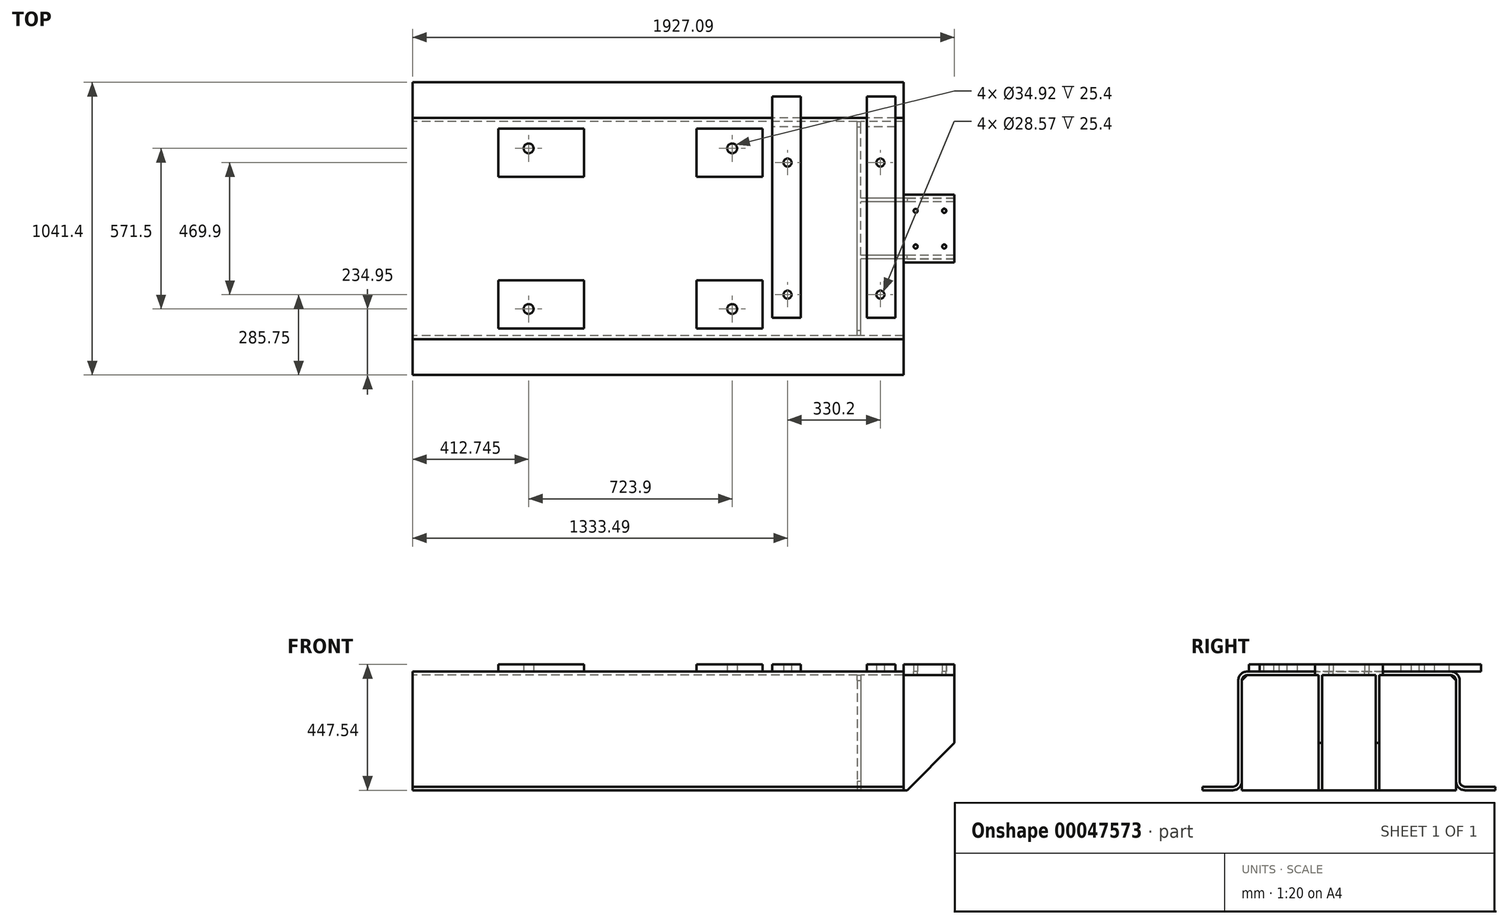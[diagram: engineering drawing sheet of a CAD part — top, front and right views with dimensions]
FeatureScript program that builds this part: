
annotation { "Feature Type Name" : "Feature", "Feature Type Description" : "" }
export const myFeature = defineFeature(function(context is Context, id is Id, definition is map)
    precondition{}
    {
        {
            var Q0;
            Q0=qCreatedBy(makeId("Right.planeOp"),FACE);
            var sketch = newSketch(context, id + "F0", { "sketchPlane" : qUnion([Q0])});
            skLineSegment(sketch, "E0.rect.bottom", {"start": v(-361.95, 211.07) * mm, "end": v(361.95, 211.07) * mm});
            skLineSegment(sketch, "E0.rect.top", {"start": v(-520.7, -211.07) * mm, "end": v(-412.75, -211.07) * mm});
            skLineSegment(sketch, "E0.rect.left", {"start": v(-393.7, 179.32) * mm, "end": v(-393.7, -179.32) * mm});
            skLineSegment(sketch, "E0.rect.right", {"start": v(393.7, 179.32) * mm, "end": v(393.7, -179.32) * mm});
            skPoint(sketch, "E0.rect.middle", {"position": v(0, 0) * mm});
            skLineSegment(sketch, "E1.0", {"start": v(-361.95, 198.37) * mm, "end": v(361.95, 198.37) * mm});
            skLineSegment(sketch, "E1.1", {"start": v(-381, 179.32) * mm, "end": v(-381, -179.32) * mm});
            skLineSegment(sketch, "E1.2", {"start": v(-520.7, -198.37) * mm, "end": v(-412.75, -198.37) * mm});
            skLineSegment(sketch, "E1.3", {"start": v(381, 179.32) * mm, "end": v(381, -179.32) * mm});
            skLineSegment(sketch, "E2.0", {"start": v(-520.7, -198.37) * mm, "end": v(-520.7, -211.07) * mm});
            skLineSegment(sketch, "E3", {"start": v(0, 0) * mm, "end": v(0, 407.59) * mm, "construction": true});
            skPoint(sketch, "E4.orphan", {"position": v(-393.7, -211.07) * mm});
            skLineSegment(sketch, "E5.MirrorCS", {"start": v(520.7, -198.37) * mm, "end": v(520.7, -211.07) * mm});
            skPoint(sketch, "E6.MirrorP", {"position": v(393.7, -211.07) * mm});
            skLineSegment(sketch, "E7.MirrorCS", {"start": v(520.7, -211.07) * mm, "end": v(412.75, -211.07) * mm});
            skLineSegment(sketch, "E8.MirrorCS", {"start": v(520.7, -198.37) * mm, "end": v(412.75, -198.37) * mm});
            skPoint(sketch, "E9.visualSharp", {"position": v(-393.7, -198.37) * mm});
            skArc(sketch, "E9.filletArc", {"start": v(-412.75, -198.37) * mm, "mid": v(-399.28, -192.8) * mm, "end": v(-393.7, -179.32) * mm});
            skPoint(sketch, "E10.visualSharp", {"position": v(-381, 198.37) * mm});
            skArc(sketch, "E10.filletArc", {"start": v(-361.95, 198.37) * mm, "mid": v(-375.42, 192.8) * mm, "end": v(-381, 179.32) * mm});
            skPoint(sketch, "E11.visualSharp", {"position": v(381, 198.37) * mm});
            skArc(sketch, "E11.filletArc", {"start": v(381, 179.32) * mm, "mid": v(375.42, 192.8) * mm, "end": v(361.95, 198.37) * mm});
            skPoint(sketch, "E12.visualSharp", {"position": v(393.7, -198.37) * mm});
            skArc(sketch, "E12.filletArc", {"start": v(393.7, -179.32) * mm, "mid": v(399.28, -192.8) * mm, "end": v(412.75, -198.37) * mm});
            skPoint(sketch, "E13.visualSharp", {"position": v(-381, -211.07) * mm});
            skArc(sketch, "E13.filletArc", {"start": v(-412.75, -211.07) * mm, "mid": v(-390.3, -201.77) * mm, "end": v(-381, -179.32) * mm});
            skPoint(sketch, "E14.visualSharp", {"position": v(-393.7, 211.07) * mm});
            skArc(sketch, "E14.filletArc", {"start": v(-361.95, 211.07) * mm, "mid": v(-384.4, 201.77) * mm, "end": v(-393.7, 179.32) * mm});
            skPoint(sketch, "E15.visualSharp", {"position": v(393.7, 211.07) * mm});
            skArc(sketch, "E15.filletArc", {"start": v(393.7, 179.32) * mm, "mid": v(384.4, 201.77) * mm, "end": v(361.95, 211.07) * mm});
            skPoint(sketch, "E16.visualSharp", {"position": v(381, -211.07) * mm});
            skArc(sketch, "E16.filletArc", {"start": v(381, -179.32) * mm, "mid": v(390.3, -201.77) * mm, "end": v(412.75, -211.07) * mm});
            skSolve(sketch);
        }
        {
            var Q0;
            Q0=qSketchRegion(id+"F0",true);
            extrude(context, id + "F1", {"entities" : qUnion([Q0]), "endBound" : BoundingType.SYMMETRIC, "depth" : 1746.25 * mm});
        }
        {
            var Q0;
            Q0=makeQuery(id+"F1.opExtrude","CAP_FACE",FACE,{"disambiguationData":[OSD([sQuery(id+"F0.wireOp",EDGE,"E0.rect.bottom"),sQuery(id+"F0.wireOp",EDGE,"E0.rect.top"),sQuery(id+"F0.wireOp",EDGE,"E0.rect.left"),sQuery(id+"F0.wireOp",EDGE,"E0.rect.right"),sQuery(id+"F0.wireOp",EDGE,"E1.0"),sQuery(id+"F0.wireOp",EDGE,"E1.1"),sQuery(id+"F0.wireOp",EDGE,"E1.2"),sQuery(id+"F0.wireOp",EDGE,"E1.3"),sQuery(id+"F0.wireOp",EDGE,"E2.0"),sQuery(id+"F0.wireOp",EDGE,"E5.MirrorCS"),sQuery(id+"F0.wireOp",EDGE,"E7.MirrorCS"),sQuery(id+"F0.wireOp",EDGE,"E8.MirrorCS"),sQuery(id+"F0.wireOp",EDGE,"E9.filletArc"),sQuery(id+"F0.wireOp",EDGE,"E10.filletArc"),sQuery(id+"F0.wireOp",EDGE,"E11.filletArc"),sQuery(id+"F0.wireOp",EDGE,"E12.filletArc"),sQuery(id+"F0.wireOp",EDGE,"E13.filletArc"),sQuery(id+"F0.wireOp",EDGE,"E14.filletArc"),sQuery(id+"F0.wireOp",EDGE,"E15.filletArc"),sQuery(id+"F0.wireOp",EDGE,"E16.filletArc")])],"isStart":false});
            cPlane(context, id + "F2", {"entities" : qUnion([Q0]), "cplaneType" : CPlaneType.OFFSET, "offset" : 152.4 * mm, "oppositeDirection" : true, "width" : 152.4 * mm, "height" : 152.4 * mm});
        }
        {
            var Q0;
            Q0=qCreatedBy(id+"F2.planeOp",FACE);
            var sketch = newSketch(context, id + "F3", { "sketchPlane" : qUnion([Q0])});
            skLineSegment(sketch, "E17.0", {"start": v(-361.95, 198.37) * mm, "end": v(361.95, 198.37) * mm});
            skLineSegment(sketch, "E18.0", {"start": v(-381, 179.32) * mm, "end": v(-381, -211.07) * mm});
            skLineSegment(sketch, "E19.0", {"start": v(381, 179.32) * mm, "end": v(381, -211.07) * mm});
            skLineSegment(sketch, "E20.0", {"start": v(-381, -211.07) * mm, "end": v(381, -211.07) * mm});
            skLineSegment(sketch, "E21", {"start": v(-381, 179.32) * mm, "end": v(-361.95, 198.37) * mm});
            skLineSegment(sketch, "E22", {"start": v(361.95, 198.37) * mm, "end": v(381, 179.32) * mm});
            skPoint(sketch, "E23.orphan", {"position": v(-412.75, -211.07) * mm});
            skPoint(sketch, "E24.orphan", {"position": v(381, -179.32) * mm});
            skPoint(sketch, "E25.orphan", {"position": v(-381, -179.32) * mm});
            skPoint(sketch, "E26.orphan", {"position": v(-520.7, -211.07) * mm});
            skSolve(sketch);
        }
        {
            var Q0;
            Q0=qSketchRegion(id+"F3",true);
            extrude(context, id + "F4", {"entities" : qUnion([Q0]), "oppositeDirection" : true, "depth" : 12.7 * mm});
        }
        {
            var Q0;
            Q0=makeQuery(id+"F1.opExtrude","SWEPT_FACE",FACE,{"disambiguationData":[OSD([sQuery(id+"F0.wireOp",EDGE,"E0.rect.bottom")])]});
            var sketch = newSketch(context, id + "F5", { "sketchPlane" : qUnion([Q0])});
            skLineSegment(sketch, "E27.0", {"start": v(-98.42, -361.95) * mm, "end": v(-98.42, 361.95) * mm, "construction": true});
            skLineSegment(sketch, "E28.0", {"start": v(136.53, -361.95) * mm, "end": v(136.53, 361.95) * mm, "construction": true});
            skLineSegment(sketch, "E29.0", {"start": v(371.48, -361.95) * mm, "end": v(371.48, 361.95) * mm, "construction": true});
            skLineSegment(sketch, "E30.0", {"start": v(-263.53, -361.95) * mm, "end": v(-263.53, 361.95) * mm, "construction": true});
            skLineSegment(sketch, "E31.0", {"start": v(-568.32, -361.95) * mm, "end": v(-568.32, 361.95) * mm, "construction": true});
            skLineSegment(sketch, "E32", {"start": v(-1011.97, 0) * mm, "end": v(1200.8, 0) * mm, "construction": true});
            skLineSegment(sketch, "E33.0", {"start": v(-1011.97, -184.15) * mm, "end": v(1200.8, -184.15) * mm, "construction": true});
            skLineSegment(sketch, "E34.0", {"start": v(-1011.97, -355.6) * mm, "end": v(1200.8, -355.6) * mm, "construction": true});
            skLineSegment(sketch, "E35.bottom", {"start": v(-568.32, -184.15) * mm, "end": v(-263.53, -184.15) * mm});
            skLineSegment(sketch, "E35.top", {"start": v(-568.32, -355.6) * mm, "end": v(-263.52, -355.6) * mm});
            skLineSegment(sketch, "E35.left", {"start": v(-568.32, -184.15) * mm, "end": v(-568.32, -355.6) * mm});
            skLineSegment(sketch, "E35.right", {"start": v(-263.53, -184.15) * mm, "end": v(-263.53, -355.6) * mm});
            skLineSegment(sketch, "E36.bottom", {"start": v(136.53, -184.15) * mm, "end": v(371.48, -184.15) * mm});
            skLineSegment(sketch, "E36.top", {"start": v(136.53, -355.6) * mm, "end": v(371.48, -355.6) * mm});
            skLineSegment(sketch, "E36.left", {"start": v(136.53, -184.15) * mm, "end": v(136.53, -355.6) * mm});
            skLineSegment(sketch, "E36.right", {"start": v(371.48, -184.15) * mm, "end": v(371.48, -355.6) * mm});
            skLineSegment(sketch, "E37.0", {"start": v(-460.38, -361.95) * mm, "end": v(-460.38, 361.95) * mm, "construction": true});
            skLineSegment(sketch, "E38.0", {"start": v(-1011.97, -285.75) * mm, "end": v(1200.8, -285.75) * mm, "construction": true});
            skCircle(sketch, "E39", {"center": v(-460.38, -285.75) * mm, "radius": 17.46 * mm});
            skCircle(sketch, "E40.MirrorC", {"center": v(263.53, -285.75) * mm, "radius": 17.46 * mm});
            skCircle(sketch, "E41.MirrorC", {"center": v(-460.38, 285.75) * mm, "radius": 17.46 * mm});
            skCircle(sketch, "E42.MirrorC", {"center": v(263.53, 285.75) * mm, "radius": 17.46 * mm});
            skLineSegment(sketch, "E43.MirrorCS", {"start": v(-568.32, 184.15) * mm, "end": v(-263.53, 184.15) * mm});
            skLineSegment(sketch, "E44.MirrorCS", {"start": v(-568.33, 355.6) * mm, "end": v(-263.53, 355.6) * mm});
            skLineSegment(sketch, "E45.MirrorCS", {"start": v(-568.32, 184.15) * mm, "end": v(-568.32, 355.6) * mm});
            skLineSegment(sketch, "E46.MirrorCS", {"start": v(-263.53, 184.15) * mm, "end": v(-263.53, 355.6) * mm});
            skLineSegment(sketch, "E47.MirrorCS", {"start": v(136.53, 184.15) * mm, "end": v(371.48, 184.15) * mm});
            skLineSegment(sketch, "E48.MirrorCS", {"start": v(136.52, 355.6) * mm, "end": v(371.47, 355.6) * mm});
            skLineSegment(sketch, "E49.MirrorCS", {"start": v(371.48, 184.15) * mm, "end": v(371.48, 355.6) * mm});
            skLineSegment(sketch, "E50.MirrorCS", {"start": v(136.53, 184.15) * mm, "end": v(136.52, 355.6) * mm});
            skSolve(sketch);
        }
        {
            var Q0;
            Q0=qSketchRegion(id+"F5",true);
            extrude(context, id + "F6", {"entities" : qUnion([Q0]), "operationType" : NewBodyOperationType.ADD, "depth" : 25.4 * mm});
        }
        {
            var Q0;
            Q0=makeQuery(id+"F5.imprint","IMPRINT",FACE,{"disambiguationData":[TD([[makeQuery(id+"F5.imprint","IMPRINT",EDGE,{"derivedFrom":sQuery(id+"F5.wireOp",EDGE,"E35.bottom")}),1.0]])]});
            var sketch = newSketch(context, id + "F7", { "sketchPlane" : qUnion([Q0])});
            skLineSegment(sketch, "E51.0", {"start": v(-98.42, -361.95) * mm, "end": v(-98.42, 361.95) * mm, "construction": true});
            skLineSegment(sketch, "E52.0", {"start": v(625.48, -361.95) * mm, "end": v(625.48, 361.95) * mm, "construction": true});
            skLineSegment(sketch, "E53.0", {"start": v(508.13, -317.5) * mm, "end": v(508.13, 469.9) * mm});
            skLineSegment(sketch, "E54.0", {"start": v(406.53, -317.5) * mm, "end": v(406.53, 469.9) * mm});
            skLineSegment(sketch, "E55", {"start": v(0, 0) * mm, "end": v(1304.94, 0) * mm, "construction": true});
            skLineSegment(sketch, "E56.0", {"start": v(406.53, -317.5) * mm, "end": v(508.13, -317.5) * mm});
            skLineSegment(sketch, "E57.0", {"start": v(406.53, 469.9) * mm, "end": v(508.13, 469.9) * mm});
            skLineSegment(sketch, "E58.filletArc", {"start": v(406.53, 469.9) * mm, "end": v(406.53, 469.9) * mm});
            skLineSegment(sketch, "E59.filletArc", {"start": v(508.13, 469.9) * mm, "end": v(508.13, 469.9) * mm});
            skLineSegment(sketch, "E60.filletArc", {"start": v(406.53, -317.5) * mm, "end": v(406.53, -317.5) * mm});
            skLineSegment(sketch, "E61.filletArc", {"start": v(508.13, -317.5) * mm, "end": v(508.13, -317.5) * mm});
            skLineSegment(sketch, "E62.0", {"start": v(0, 234.95) * mm, "end": v(1304.94, 234.95) * mm, "construction": true});
            skLineSegment(sketch, "E63.0", {"start": v(0, -234.95) * mm, "end": v(1304.94, -234.95) * mm, "construction": true});
            skLineSegment(sketch, "E64.0", {"start": v(460.38, -361.95) * mm, "end": v(460.38, 361.95) * mm, "construction": true});
            skCircle(sketch, "E65", {"center": v(460.38, -234.95) * mm, "radius": 14.29 * mm});
            skCircle(sketch, "E66", {"center": v(460.38, 234.95) * mm, "radius": 14.29 * mm});
            skLineSegment(sketch, "E67.MirrorCS", {"start": v(742.82, -317.5) * mm, "end": v(742.82, -317.5) * mm});
            skCircle(sketch, "E68.MirrorC", {"center": v(790.58, -234.95) * mm, "radius": 14.29 * mm});
            skCircle(sketch, "E69.MirrorC", {"center": v(790.58, 234.95) * mm, "radius": 14.29 * mm});
            skLineSegment(sketch, "E70.MirrorCS", {"start": v(742.82, 469.9) * mm, "end": v(742.82, 469.9) * mm});
            skLineSegment(sketch, "E71.MirrorCS", {"start": v(844.42, 469.9) * mm, "end": v(844.42, 469.9) * mm});
            skLineSegment(sketch, "E72.MirrorCS", {"start": v(742.82, -317.5) * mm, "end": v(742.82, 469.9) * mm});
            skLineSegment(sketch, "E73.MirrorCS", {"start": v(844.42, -317.5) * mm, "end": v(844.42, 469.9) * mm});
            skLineSegment(sketch, "E74.MirrorCS", {"start": v(844.42, -317.5) * mm, "end": v(742.82, -317.5) * mm});
            skLineSegment(sketch, "E75.MirrorCS", {"start": v(844.42, 469.9) * mm, "end": v(742.82, 469.9) * mm});
            skLineSegment(sketch, "E76.MirrorCS", {"start": v(844.42, -317.5) * mm, "end": v(844.42, -317.5) * mm});
            skSolve(sketch);
        }
        {
            var Q0;
            Q0=qSketchRegion(id+"F7",true);
            extrude(context, id + "F8", {"entities" : qUnion([Q0]), "operationType" : NewBodyOperationType.ADD, "depth" : 25.4 * mm});
        }
        {
            var Q0;
            {var subQ0=sQuery(id+"F0.wireOp",EDGE,"E0.rect.bottom");var subQ32=sQuery(id+"F0.wireOp",EDGE,"E14.filletArc");var subQ35=makeQuery(id+"F1.opExtrude","SWEPT_FACE",FACE,{"disambiguationData":[OSD([subQ32])]});Q0=makeQuery(id+"F8.boolean.opBoolean","SPLIT",FACE,{"disambiguationData":[TD([subQ35])],"derivedFrom":makeQuery(id+"F6.boolean.opBoolean","SPLIT",FACE,{"disambiguationData":[TD([subQ35])],"derivedFrom":makeQuery(id+"F1.opExtrude","SWEPT_FACE",FACE,{"disambiguationData":[OSD([subQ0])]})})});}
            var sketch = newSketch(context, id + "F9", { "sketchPlane" : qUnion([Q0])});
            skLineSegment(sketch, "E77.0.0", {"start": v(742.82, 469.9) * mm, "end": v(742.82, -317.5) * mm, "construction": true});
            skLineSegment(sketch, "E77.0.1", {"start": v(742.82, -317.5) * mm, "end": v(844.42, -317.5) * mm, "construction": true});
            skLineSegment(sketch, "E77.0.2", {"start": v(844.42, -317.5) * mm, "end": v(844.42, 469.9) * mm, "construction": true});
            skLineSegment(sketch, "E77.0.3", {"start": v(844.42, 469.9) * mm, "end": v(742.82, 469.9) * mm, "construction": true});
            skLineSegment(sketch, "E78.0", {"start": v(1053.97, 469.9) * mm, "end": v(1053.97, -317.5) * mm, "construction": true});
            skLineSegment(sketch, "E79", {"start": v(0, 0) * mm, "end": v(1391.66, 0) * mm, "construction": true});
            skLineSegment(sketch, "E80.0", {"start": v(0, 120.65) * mm, "end": v(1391.66, 120.65) * mm});
            skLineSegment(sketch, "E81.0", {"start": v(708.02, -361.95) * mm, "end": v(708.02, 361.95) * mm, "construction": true});
            skLineSegment(sketch, "E82.0", {"start": v(720.73, -361.95) * mm, "end": v(720.73, 361.95) * mm, "construction": true});
            skLineSegment(sketch, "E83.0", {"start": v(873.12, -361.95) * mm, "end": v(873.12, 361.95) * mm, "construction": true});
            skLineSegment(sketch, "E84.bottom", {"start": v(873.12, 120.65) * mm, "end": v(1053.97, 120.65) * mm});
            skLineSegment(sketch, "E84.top", {"start": v(873.12, -120.65) * mm, "end": v(1053.97, -120.65) * mm});
            skLineSegment(sketch, "E84.left", {"start": v(873.12, 120.65) * mm, "end": v(873.12, -120.65) * mm});
            skLineSegment(sketch, "E84.right", {"start": v(1053.97, 120.65) * mm, "end": v(1053.97, -120.65) * mm});
            skSolve(sketch);
        }
        {
            var Q0;
            Q0=qSketchRegion(id+"F9",true);
            extrude(context, id + "F10", {"entities" : qUnion([Q0]), "operationType" : NewBodyOperationType.ADD, "oppositeDirection" : true, "depth" : 12.7 * mm});
        }
        {
            var Q0;
            Q0=qCreatedBy(makeId("Front.planeOp"),FACE);
            cPlane(context, id + "F11", {"entities" : qUnion([Q0]), "cplaneType" : CPlaneType.OFFSET, "offset" : 95.25 * mm, "oppositeDirection" : true, "width" : 152.4 * mm, "height" : 152.4 * mm});
        }
        {
            var Q0;
            Q0=qCreatedBy(id+"F11.planeOp",FACE);
            var sketch = newSketch(context, id + "F12", { "sketchPlane" : qUnion([Q0])});
            skLineSegment(sketch, "E85.0", {"start": v(873.12, 198.37) * mm, "end": v(1053.97, 198.37) * mm, "construction": true});
            skPoint(sketch, "E86.0", {"position": v(720.73, 179.32) * mm});
            skLineSegment(sketch, "E87", {"start": v(720.73, 179.32) * mm, "end": v(720.73, -266.28) * mm, "construction": true});
            skLineSegment(sketch, "E88.0", {"start": v(873.12, -211.07) * mm, "end": v(-873.12, -211.07) * mm, "construction": true});
            skLineSegment(sketch, "E89.bottom", {"start": v(1053.97, 198.37) * mm, "end": v(720.73, 198.37) * mm});
            skLineSegment(sketch, "E89.top", {"start": v(1053.97, -211.07) * mm, "end": v(720.73, -211.07) * mm});
            skLineSegment(sketch, "E89.left", {"start": v(1053.97, 198.37) * mm, "end": v(1053.97, -211.07) * mm});
            skLineSegment(sketch, "E89.right", {"start": v(720.73, 198.37) * mm, "end": v(720.73, -211.07) * mm});
            skSolve(sketch);
        }
        {
            var Q0;
            Q0=qSketchRegion(id+"F12",true);
            extrude(context, id + "F13", {"entities" : qUnion([Q0]), "oppositeDirection" : true, "depth" : 12.7 * mm});
        }
        {
            var Q0;
            Q0=makeQuery(id+"F13.opExtrude","SWEPT_EDGE",EDGE,{"disambiguationData":[OSD([sQuery(id+"F12.wireOp",EDGE,"E89.top"),sQuery(id+"F12.wireOp",EDGE,"E89.left")])]});
            chamfer(context, id + "F14", {"entities" : qUnion([Q0]), "width" : 168.15 * mm, "tangentPropagation" : true});
        }
        {
            var Q0;
            Q0=makeQuery(id+"F13.opExtrude","SWEPT_BODY",BODY,{"disambiguationData":[OSD([sQuery(id+"F12.wireOp",EDGE,"E89.bottom"),sQuery(id+"F12.wireOp",EDGE,"E89.top"),sQuery(id+"F12.wireOp",EDGE,"E89.left"),sQuery(id+"F12.wireOp",EDGE,"E89.right")])]});
            var Q1;
            Q1=qCreatedBy(makeId("Front.planeOp"),FACE);
            mirror(context, id + "F15", {"operationType" : NewBodyOperationType.ADD, "entities" : qUnion([Q0]), "mirrorPlane" : qUnion([Q1])});
        }
        {
            var Q0;
            {var subQ0=sQuery(id+"F0.wireOp",EDGE,"E0.rect.bottom");var subQ32=sQuery(id+"F0.wireOp",EDGE,"E14.filletArc");var subQ35=makeQuery(id+"F1.opExtrude","SWEPT_FACE",FACE,{"disambiguationData":[OSD([subQ32])]});Q0=makeQuery(id+"F10.boolean.opBoolean","MERGE",FACE,{"derivedFrom":[makeQuery(id+"F8.boolean.opBoolean","SPLIT",FACE,{"disambiguationData":[TD([subQ35])],"derivedFrom":makeQuery(id+"F6.boolean.opBoolean","SPLIT",FACE,{"disambiguationData":[TD([subQ35])],"derivedFrom":makeQuery(id+"F1.opExtrude","SWEPT_FACE",FACE,{"disambiguationData":[OSD([subQ0])]})})}),makeQuery(id+"F10.opExtrude","CAP_FACE",FACE,{"disambiguationData":[OSD([sQuery(id+"F9.wireOp",EDGE,"E84.bottom"),sQuery(id+"F9.wireOp",EDGE,"E84.top"),sQuery(id+"F9.wireOp",EDGE,"E84.left"),sQuery(id+"F9.wireOp",EDGE,"E84.right")])],"isStart":true})]});}
            var sketch = newSketch(context, id + "F16", { "sketchPlane" : qUnion([Q0])});
            skLineSegment(sketch, "E90", {"start": v(0, 0) * mm, "end": v(1237.02, 0) * mm, "construction": true});
            skLineSegment(sketch, "E91.0", {"start": v(625.48, -361.95) * mm, "end": v(625.48, 361.95) * mm, "construction": true});
            skLineSegment(sketch, "E92.0", {"start": v(916.05, -361.95) * mm, "end": v(916.05, 361.95) * mm, "construction": true});
            skLineSegment(sketch, "E93.0", {"start": v(1017.65, -361.95) * mm, "end": v(1017.65, 361.95) * mm, "construction": true});
            skLineSegment(sketch, "E94.0", {"start": v(0, -63.5) * mm, "end": v(1237.02, -63.5) * mm, "construction": true});
            skLineSegment(sketch, "E95.0", {"start": v(0, 63.5) * mm, "end": v(1237.02, 63.5) * mm, "construction": true});
            skCircle(sketch, "E96", {"center": v(916.05, 63.5) * mm, "radius": 7.14 * mm});
            skCircle(sketch, "E97", {"center": v(1017.65, 63.5) * mm, "radius": 7.14 * mm});
            skCircle(sketch, "E98", {"center": v(1017.65, -63.5) * mm, "radius": 7.14 * mm});
            skCircle(sketch, "E99", {"center": v(916.05, -63.5) * mm, "radius": 7.14 * mm});
            skSolve(sketch);
        }
        {
            var Q0;
            Q0=qSketchRegion(id+"F16",true);
            extrude(context, id + "F17", {"entities" : qUnion([Q0]), "operationType" : NewBodyOperationType.REMOVE, "endBound" : BoundingType.THROUGH_ALL, "oppositeDirection" : true, "depth" : 25.4 * mm});
        }
        {
            var Q0;
            {var subQ0=sQuery(id+"F0.wireOp",EDGE,"E0.rect.bottom");var subQ32=sQuery(id+"F0.wireOp",EDGE,"E14.filletArc");var subQ35=makeQuery(id+"F1.opExtrude","SWEPT_FACE",FACE,{"disambiguationData":[OSD([subQ32])]});Q0=makeQuery(id+"F10.boolean.opBoolean","MERGE",FACE,{"derivedFrom":[makeQuery(id+"F8.boolean.opBoolean","SPLIT",FACE,{"disambiguationData":[TD([subQ35])],"derivedFrom":makeQuery(id+"F6.boolean.opBoolean","SPLIT",FACE,{"disambiguationData":[TD([subQ35])],"derivedFrom":makeQuery(id+"F1.opExtrude","SWEPT_FACE",FACE,{"disambiguationData":[OSD([subQ0])]})})}),makeQuery(id+"F10.opExtrude","CAP_FACE",FACE,{"disambiguationData":[OSD([sQuery(id+"F9.wireOp",EDGE,"E84.bottom"),sQuery(id+"F9.wireOp",EDGE,"E84.top"),sQuery(id+"F9.wireOp",EDGE,"E84.left"),sQuery(id+"F9.wireOp",EDGE,"E84.right")])],"isStart":true})]});}
            var sketch = newSketch(context, id + "F18", { "sketchPlane" : qUnion([Q0])});
            skLineSegment(sketch, "E100.bottom", {"start": v(1053.97, 120.65) * mm, "end": v(873.12, 120.65) * mm});
            skLineSegment(sketch, "E100.top", {"start": v(1053.97, -120.65) * mm, "end": v(873.12, -120.65) * mm});
            skLineSegment(sketch, "E100.left", {"start": v(1053.97, 120.65) * mm, "end": v(1053.97, -120.65) * mm});
            skLineSegment(sketch, "E100.right", {"start": v(873.12, 120.65) * mm, "end": v(873.12, -120.65) * mm});
            skCircle(sketch, "E101", {"center": v(916.05, 63.5) * mm, "radius": 7.13 * mm});
            skCircle(sketch, "E102", {"center": v(1017.65, 63.5) * mm, "radius": 7.46 * mm});
            skCircle(sketch, "E103", {"center": v(916.05, -63.5) * mm, "radius": 7.32 * mm});
            skCircle(sketch, "E104", {"center": v(1017.65, -63.5) * mm, "radius": 7.25 * mm});
            skSolve(sketch);
        }
        {
            var Q0;
            Q0=qSketchRegion(id+"F18",true);
            extrude(context, id + "F19", {"entities" : qUnion([Q0]), "operationType" : NewBodyOperationType.ADD, "depth" : 25.4 * mm});
        }
    });
